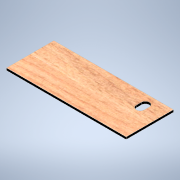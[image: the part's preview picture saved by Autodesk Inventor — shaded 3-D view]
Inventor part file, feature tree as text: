
AUTODESK INVENTOR PART (.ipt)
format: ipt  version: 2021 (Build 250183000, 183)  size: 123,904 bytes
history: native  units: mm
features: extrude x1, sketch x1
ambient origin geometry x8: Origin, YZ Plane, XZ Plane, XY Plane, X Axis, Y Axis, Z Axis, Center Point
bodies: Volumenkörper1 (feature_tree)
feature tree (2):
  extrude  "Extrusion1"  Depth=65.5mm
  sketch  "Skizze1"  dims[d0=165.5mm d1=65.5mm d2=3.0mm d3=0.0mm d8=11.0mm d9=7.0mm d10=13.5mm d11=20.0mm]
